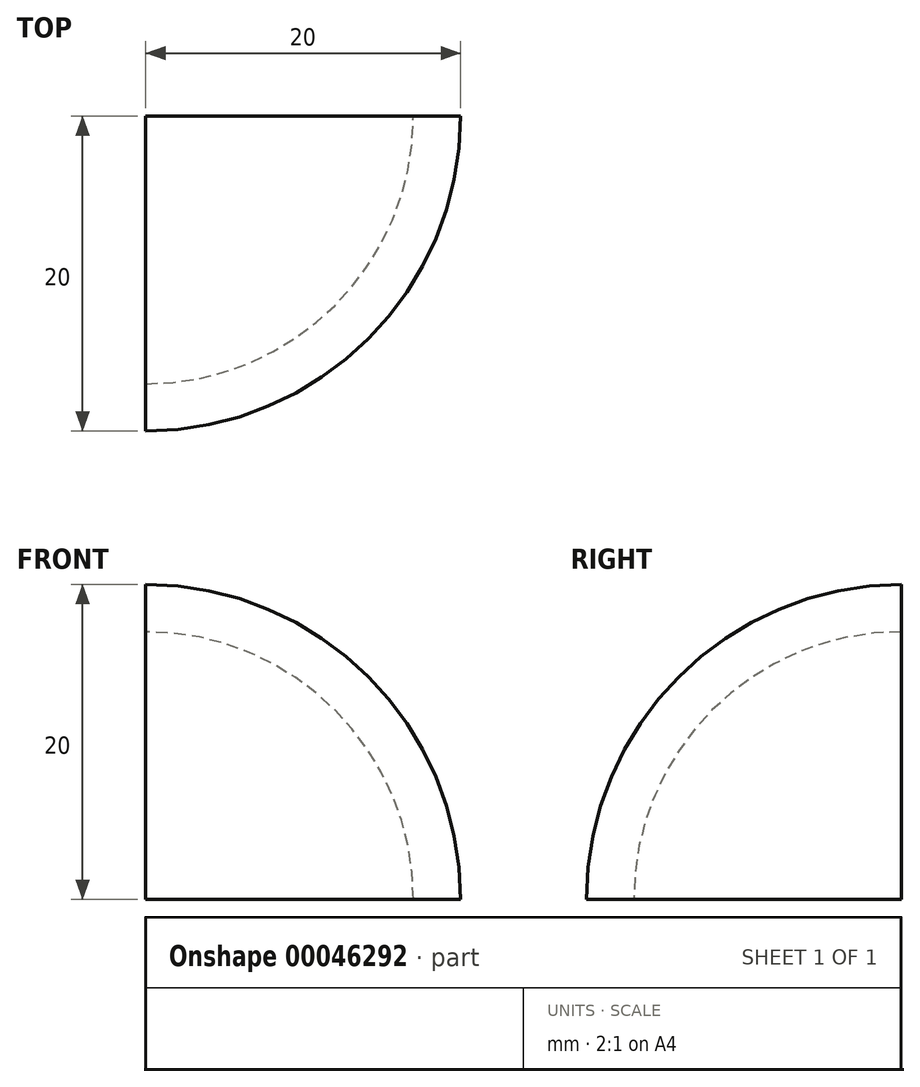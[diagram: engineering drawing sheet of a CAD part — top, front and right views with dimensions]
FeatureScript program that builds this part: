
annotation { "Feature Type Name" : "Feature", "Feature Type Description" : "" }
export const myFeature = defineFeature(function(context is Context, id is Id, definition is map)
    precondition{}
    {
        {
            var Q0;
            Q0=qCreatedBy(makeId("Front.planeOp"),FACE);
            var sketch = newSketch(context, id + "F0", { "sketchPlane" : qUnion([Q0])});
            skArc(sketch, "E0", {"start": v(20, 0) * mm, "mid": v(14.14, 14.14) * mm, "end": v(0, 20) * mm});
            skLineSegment(sketch, "E1", {"start": v(0, 20) * mm, "end": v(0, 0) * mm});
            skLineSegment(sketch, "E2", {"start": v(0, 0) * mm, "end": v(20, 0) * mm});
            skArc(sketch, "E3.0", {"start": v(17, 0) * mm, "mid": v(12.02, 12.02) * mm, "end": v(0, 17) * mm});
            skSolve(sketch);
        }
        {
            var Q0;
            Q0 = qSketchRegion(id + "F0", true);
            var Q1;
            Q1=sQuery(id+"F0.wireOp",EDGE,"E1");
            revolve(context, id + "F1", {"entities" : qUnion([Q0]), "axis" : qUnion([Q1]), "revolveType" : RevolveType.ONE_DIRECTION, "angle" : 90 * degree});
        }
        {
            var Q0;
            {var subQ3=sQuery(id+"F0.wireOp",EDGE,"E3.0");Q0=makeQuery(id+"F0.imprint","IMPRINT",FACE,{"disambiguationData":[TD([[makeQuery(id+"F0.imprint","IMPRINT",EDGE,{"derivedFrom":subQ3}),1.0]])]});}
            var Q1;
            Q1=sQuery(id+"F0.wireOp",EDGE,"E1");
            revolve(context, id + "F2", {"operationType" : NewBodyOperationType.REMOVE, "entities" : qUnion([Q0]), "axis" : qUnion([Q1]), "revolveType" : RevolveType.ONE_DIRECTION, "angle" : 90 * degree});
        }
    });
